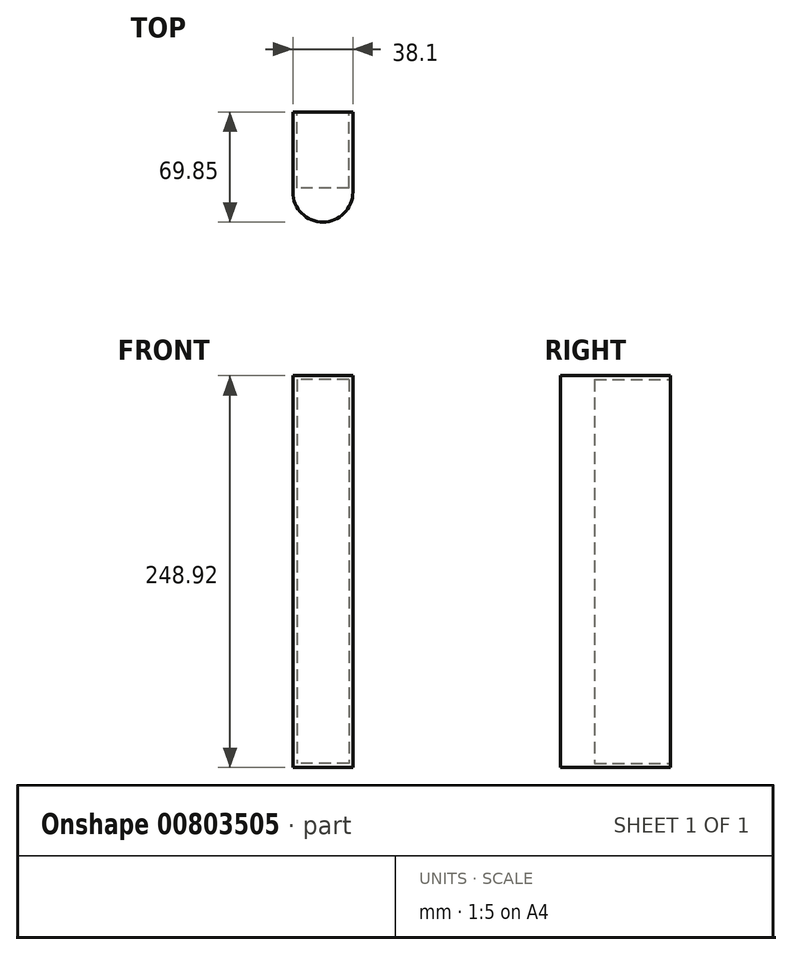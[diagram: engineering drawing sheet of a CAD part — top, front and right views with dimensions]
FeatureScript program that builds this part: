
annotation { "Feature Type Name" : "Feature", "Feature Type Description" : "" }
export const myFeature = defineFeature(function(context is Context, id is Id, definition is map)
    precondition{}
    {
        {
            var Q0;
            Q0=qCreatedBy(makeId("Top.planeOp"),FACE);
            var sketch = newSketch(context, id + "F0", { "sketchPlane" : qUnion([Q0])});
            skCircle(sketch, "E0", {"center": v(0, 0) * mm, "radius": 19.05 * mm});
            skLineSegment(sketch, "E1.bottom", {"start": v(-19.05, 0) * mm, "end": v(19.05, 0) * mm});
            skLineSegment(sketch, "E1.top", {"start": v(-19.05, 50.8) * mm, "end": v(19.05, 50.8) * mm});
            skLineSegment(sketch, "E1.left", {"start": v(-19.05, 0) * mm, "end": v(-19.05, 50.8) * mm});
            skLineSegment(sketch, "E1.right", {"start": v(19.05, 0) * mm, "end": v(19.05, 50.8) * mm});
            skSolve(sketch);
        }
        {
            var Q0;
            Q0=makeQuery(id+"F0.imprint","IMPRINT",FACE,{"disambiguationData":[TD([[makeQuery(id+"F0.imprint","IMPRINT",EDGE,{"derivedFrom":sQuery(id+"F0.wireOp",EDGE,"E1.top")}),-1.0]])]});
            var Q1;
            {var subQ0=sQuery(id+"F0.wireOp",EDGE,"E1.bottom");Q1=makeQuery(id+"F0.imprint","IMPRINT",FACE,{"disambiguationData":[TD([[makeQuery(id+"F0.imprint","IMPRINT",EDGE,{"derivedFrom":subQ0}),1.0]])]});}
            var Q2;
            {var subQ0=sQuery(id+"F0.wireOp",EDGE,"E1.bottom");Q2=makeQuery(id+"F0.imprint","IMPRINT",FACE,{"disambiguationData":[TD([[makeQuery(id+"F0.imprint","IMPRINT",EDGE,{"derivedFrom":subQ0}),-1.0]])]});}
            extrude(context, id + "F1", {"entities" : qUnion([Q0, Q1, Q2]), "depth" : 248.92 * mm, "offsetDistance" : 25.4 * mm});
        }
        {
            var Q0;
            Q0=makeQuery(id+"F1.opExtrude","SWEPT_FACE",FACE,{"disambiguationData":[OSD([sQuery(id+"F0.wireOp",EDGE,"E1.top")])]});
            var sketch = newSketch(context, id + "F2", { "sketchPlane" : qUnion([Q0])});
            skLineSegment(sketch, "E2.bottom", {"start": v(-16.51, 246.38) * mm, "end": v(16.5, 246.38) * mm});
            skLineSegment(sketch, "E2.top", {"start": v(-16.5, 2.54) * mm, "end": v(16.51, 2.54) * mm});
            skLineSegment(sketch, "E2.left", {"start": v(-16.5, 246.38) * mm, "end": v(-16.5, 2.54) * mm});
            skLineSegment(sketch, "E2.right", {"start": v(16.51, 246.38) * mm, "end": v(16.51, 2.54) * mm});
            skSolve(sketch);
        }
        {
            var Q0;
            Q0=makeQuery(id+"F2.imprint","IMPRINT",FACE,{"disambiguationData":[TD([[makeQuery(id+"F2.imprint","IMPRINT",EDGE,{"derivedFrom":sQuery(id+"F2.wireOp",EDGE,"E2.bottom")}),-1.0]])]});
            extrude(context, id + "F3", {"entities" : qUnion([Q0]), "operationType" : NewBodyOperationType.REMOVE, "oppositeDirection" : true, "depth" : 48.26 * mm, "offsetDistance" : 25.4 * mm});
        }
    });
